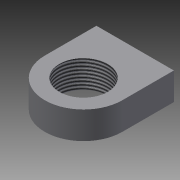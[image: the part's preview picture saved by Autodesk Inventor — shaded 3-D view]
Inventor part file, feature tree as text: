
AUTODESK INVENTOR PART (.ipt)
format: ipt  version: 2013 (Build 170138000, 138)  size: 84,992 bytes
history: native  units: in
note: dims shown in document units (in); Inventor stores cm internally (conversion verified against a paired STEP export)
features: extrude x1, thread x1, sketch x1
ambient origin geometry x8: Origin, YZ Plane, XZ Plane, XY Plane, X Axis, Y Axis, Z Axis, Center Point
bodies: Solid1 (feature_tree)
feature tree (3):
  extrude  "Extrusion1"  Depth=1.5in
  thread  "Thread1"  [1 undecoded]
  sketch  "Sketch1"  dims[d0=0.9375in d2=1.5in d3=0.53in d4=0.0in d5=1.0in d6=0.0in d16=1.0in]
note: 1 required parameter value undecoded (feature->parameter linkage not recoverable at this tier; creation-order binding heuristic only, values carry confidence <= 0.55)
